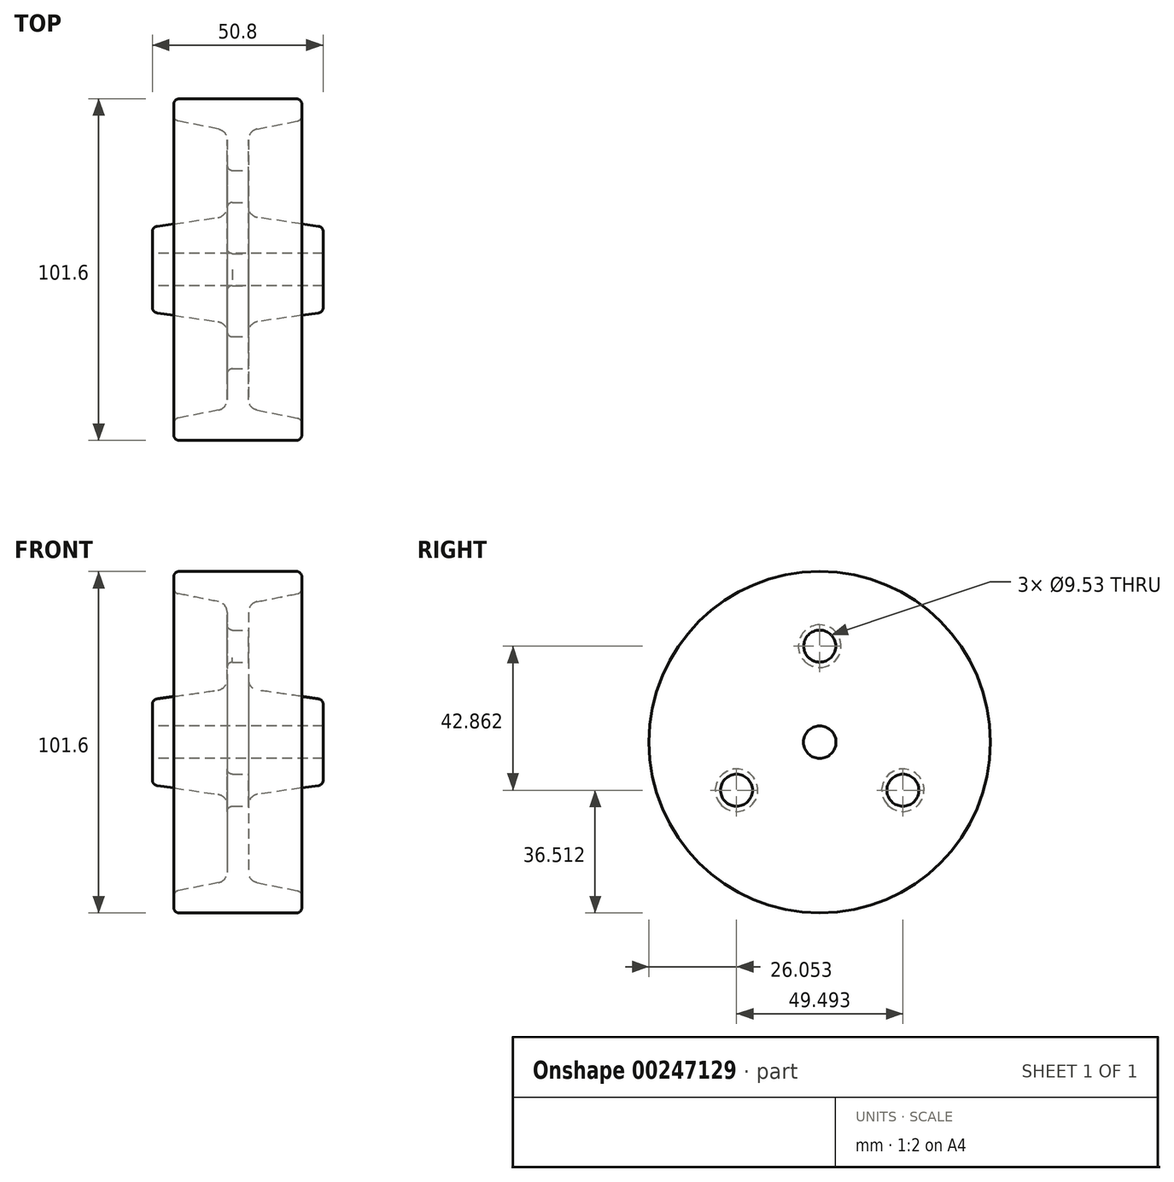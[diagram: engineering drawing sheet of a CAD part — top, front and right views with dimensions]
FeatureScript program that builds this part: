
annotation { "Feature Type Name" : "Feature", "Feature Type Description" : "" }
export const myFeature = defineFeature(function(context is Context, id is Id, definition is map)
    precondition{}
    {
        {
            var Q0;
            Q0=qCreatedBy(makeId("Front.planeOp"),FACE);
            var sketch = newSketch(context, id + "F0", { "sketchPlane" : qUnion([Q0])});
            skLineSegment(sketch, "E0", {"start": v(-25.03, 50.8) * mm, "end": v(9.9, 50.8) * mm});
            skLineSegment(sketch, "E1", {"start": v(-32.97, 4.83) * mm, "end": v(17.83, 4.83) * mm});
            skPoint(sketch, "E2", {"position": v(-7.57, 50.8) * mm});
            skPoint(sketch, "E3", {"position": v(-7.57, 4.83) * mm});
            skLineSegment(sketch, "E4", {"start": v(-32.97, 4.83) * mm, "end": v(-32.97, 11.32) * mm});
            skLineSegment(sketch, "E5", {"start": v(-26.62, 49.21) * mm, "end": v(-26.62, 45.75) * mm});
            skLineSegment(sketch, "E6", {"start": v(-7.57, 4.83) * mm, "end": v(-10.75, 4.83) * mm});
            skLineSegment(sketch, "E7", {"start": v(-7.57, 4.83) * mm, "end": v(-4.4, 4.83) * mm});
            skLineSegment(sketch, "E8", {"start": v(-31.6, 12.9) * mm, "end": v(-13.47, 15.49) * mm});
            skLineSegment(sketch, "E9", {"start": v(17.83, 4.83) * mm, "end": v(17.83, 11.32) * mm});
            skLineSegment(sketch, "E10", {"start": v(-1.67, 15.49) * mm, "end": v(16.47, 12.9) * mm});
            skLineSegment(sketch, "E11", {"start": v(-7.57, 50.8) * mm, "end": v(-10.75, 50.8) * mm});
            skLineSegment(sketch, "E12", {"start": v(-7.57, 50.8) * mm, "end": v(-4.4, 50.8) * mm});
            skLineSegment(sketch, "E13", {"start": v(-13.3, 41.79) * mm, "end": v(-25.35, 44.2) * mm});
            skLineSegment(sketch, "E14", {"start": v(11.48, 49.21) * mm, "end": v(11.48, 45.75) * mm});
            skLineSegment(sketch, "E15", {"start": v(-1.84, 41.79) * mm, "end": v(10.2, 44.2) * mm});
            skLineSegment(sketch, "E16", {"start": v(-10.75, 38.67) * mm, "end": v(-10.75, 34.92) * mm});
            skPoint(sketch, "E17.startSnap0", {"position": v(-10.75, 28.58) * mm});
            skLineSegment(sketch, "E18", {"start": v(-32.97, 4.83) * mm, "end": v(-32.97, 0) * mm});
            skLineSegment(sketch, "E19", {"start": v(-4.4, 18.63) * mm, "end": v(-4.4, 22.23) * mm});
            skLineSegment(sketch, "E20", {"start": v(-4.4, 38.67) * mm, "end": v(-4.4, 34.92) * mm});
            skLineSegment(sketch, "E21", {"start": v(-5.98, 33.34) * mm, "end": v(-9.16, 33.34) * mm});
            skLineSegment(sketch, "E22", {"start": v(-5.98, 23.81) * mm, "end": v(-9.16, 23.81) * mm});
            skLineSegment(sketch, "E23.trimOffspring", {"start": v(-10.75, 22.22) * mm, "end": v(-10.75, 18.63) * mm});
            skLineSegment(sketch, "E24", {"start": v(17.83, 4.83) * mm, "end": v(17.83, 0) * mm});
            skPoint(sketch, "E25.visualSharp", {"position": v(-10.75, 41.28) * mm});
            skArc(sketch, "E25.filletArc", {"start": v(-10.75, 38.67) * mm, "mid": v(-11.47, 40.69) * mm, "end": v(-13.3, 41.79) * mm});
            skPoint(sketch, "E26.visualSharp", {"position": v(-4.4, 41.28) * mm});
            skArc(sketch, "E26.filletArc", {"start": v(-1.84, 41.79) * mm, "mid": v(-3.68, 40.69) * mm, "end": v(-4.4, 38.67) * mm});
            skPoint(sketch, "E27.visualSharp", {"position": v(-4.4, 15.88) * mm});
            skArc(sketch, "E27.filletArc", {"start": v(-4.4, 18.63) * mm, "mid": v(-3.62, 16.55) * mm, "end": v(-1.67, 15.49) * mm});
            skPoint(sketch, "E28.visualSharp", {"position": v(-10.75, 15.88) * mm});
            skArc(sketch, "E28.filletArc", {"start": v(-13.47, 15.49) * mm, "mid": v(-11.52, 16.55) * mm, "end": v(-10.75, 18.63) * mm});
            skLineSegment(sketch, "E29", {"start": v(-32.97, 0) * mm, "end": v(-24.37, 0) * mm});
            skPoint(sketch, "E30.visualSharp", {"position": v(-26.62, 50.8) * mm});
            skArc(sketch, "E30.filletArc", {"start": v(-25.03, 50.8) * mm, "mid": v(-26.16, 50.34) * mm, "end": v(-26.62, 49.21) * mm});
            skPoint(sketch, "E31.visualSharp", {"position": v(-26.62, 44.45) * mm});
            skArc(sketch, "E31.filletArc", {"start": v(-26.62, 45.75) * mm, "mid": v(-26.26, 44.74) * mm, "end": v(-25.35, 44.2) * mm});
            skPoint(sketch, "E32.visualSharp", {"position": v(11.48, 50.8) * mm});
            skArc(sketch, "E32.filletArc", {"start": v(11.48, 49.21) * mm, "mid": v(11.01, 50.34) * mm, "end": v(9.9, 50.8) * mm});
            skPoint(sketch, "E33.visualSharp", {"position": v(11.48, 44.45) * mm});
            skArc(sketch, "E33.filletArc", {"start": v(10.2, 44.2) * mm, "mid": v(11.12, 44.74) * mm, "end": v(11.48, 45.75) * mm});
            skPoint(sketch, "E34.visualSharp", {"position": v(-10.75, 33.34) * mm});
            skArc(sketch, "E34.filletArc", {"start": v(-10.75, 34.92) * mm, "mid": v(-10.28, 33.8) * mm, "end": v(-9.16, 33.34) * mm});
            skPoint(sketch, "E35.visualSharp", {"position": v(-4.4, 33.34) * mm});
            skArc(sketch, "E35.filletArc", {"start": v(-5.98, 33.34) * mm, "mid": v(-4.86, 33.8) * mm, "end": v(-4.4, 34.92) * mm});
            skPoint(sketch, "E36.visualSharp", {"position": v(-10.75, 23.81) * mm});
            skArc(sketch, "E36.filletArc", {"start": v(-9.16, 23.81) * mm, "mid": v(-10.28, 23.35) * mm, "end": v(-10.75, 22.22) * mm});
            skPoint(sketch, "E37.visualSharp", {"position": v(-4.4, 23.81) * mm});
            skArc(sketch, "E37.filletArc", {"start": v(-4.4, 22.23) * mm, "mid": v(-4.86, 23.35) * mm, "end": v(-5.98, 23.81) * mm});
            skPoint(sketch, "E38.visualSharp", {"position": v(-32.97, 12.7) * mm});
            skArc(sketch, "E38.filletArc", {"start": v(-31.6, 12.9) * mm, "mid": v(-32.58, 12.36) * mm, "end": v(-32.97, 11.32) * mm});
            skPoint(sketch, "E39.visualSharp", {"position": v(17.83, 12.7) * mm});
            skArc(sketch, "E39.filletArc", {"start": v(17.83, 11.32) * mm, "mid": v(17.44, 12.36) * mm, "end": v(16.47, 12.9) * mm});
            skLineSegment(sketch, "E40", {"start": v(-10.75, 34.92) * mm, "end": v(-10.75, 22.22) * mm});
            skLineSegment(sketch, "E41", {"start": v(-4.4, 34.92) * mm, "end": v(-4.4, 22.23) * mm});
            skSolve(sketch);
        }
        {
            var Q0;
            Q0 = qSketchRegion(id + "F0", true);
            var Q1;
            Q1=sQuery(id+"F0.wireOp",EDGE,"E29");
            revolve(context, id + "F1", {"entities" : qUnion([Q0]), "axis" : qUnion([Q1]), "revolveType" : RevolveType.FULL});
        }
        {
            var Q0;
            Q0=makeQuery(id+"F1.opRevolve","SWEPT_FACE",FACE,{"disambiguationData":[OSD([sQuery(id+"F0.wireOp",EDGE,"E19"),sQuery(id+"F0.wireOp",EDGE,"E20"),sQuery(id+"F0.wireOp",EDGE,"E41")])]});
            var sketch = newSketch(context, id + "F2", { "sketchPlane" : qUnion([Q0])});
            skArc(sketch, "E42", {"start": v(-4.75, 28.18) * mm, "mid": v(-24.75, 14.29) * mm, "end": v(-26.78, -9.98) * mm});
            skCircle(sketch, "E43", {"center": v(0, 28.58) * mm, "radius": 4.76 * mm});
            skCircle(sketch, "E44.1.0", {"center": v(-24.75, -14.29) * mm, "radius": 4.76 * mm});
            skCircle(sketch, "E44.2.0", {"center": v(24.75, -14.29) * mm, "radius": 4.76 * mm});
            skArc(sketch, "E45.trimOffspring", {"start": v(-22.03, -18.2) * mm, "mid": v(0, -28.58) * mm, "end": v(22.03, -18.2) * mm});
            skArc(sketch, "E46.trimOffspring", {"start": v(26.78, -9.98) * mm, "mid": v(24.75, 14.29) * mm, "end": v(4.75, 28.18) * mm});
            skSolve(sketch);
        }
        {
            var Q0;
            {var subQ0=sQuery(id+"F2.wireOp",EDGE,"E43");var subQ1=makeQuery(id+"F2.imprint","INTERSECT",VERTEX,{"derivedFrom":[sQuery(id+"F2.wireOp",EDGE,"E42"),subQ0]});Q0=makeQuery(id+"F2.imprint","IMPRINT",FACE,{"disambiguationData":[TD([[makeQuery(id+"F2.imprint","IMPRINT",EDGE,{"disambiguationData":[TD([[subQ1,-1.0]])],"derivedFrom":subQ0}),1.0]])]});}
            var Q1;
            {var subQ0=sQuery(id+"F2.wireOp",EDGE,"E44.2.0");var subQ1=makeQuery(id+"F2.imprint","INTERSECT",VERTEX,{"derivedFrom":[subQ0,sQuery(id+"F2.wireOp",EDGE,"E45.trimOffspring")]});Q1=makeQuery(id+"F2.imprint","IMPRINT",FACE,{"disambiguationData":[TD([[makeQuery(id+"F2.imprint","IMPRINT",EDGE,{"disambiguationData":[TD([[subQ1,1.0]])],"derivedFrom":subQ0}),1.0]])]});}
            var Q2;
            {var subQ0=sQuery(id+"F2.wireOp",EDGE,"E44.1.0");var subQ1=makeQuery(id+"F2.imprint","INTERSECT",VERTEX,{"derivedFrom":[sQuery(id+"F2.wireOp",EDGE,"E42"),subQ0]});Q2=makeQuery(id+"F2.imprint","IMPRINT",FACE,{"disambiguationData":[TD([[makeQuery(id+"F2.imprint","IMPRINT",EDGE,{"disambiguationData":[TD([[subQ1,1.0]])],"derivedFrom":subQ0}),1.0]])]});}
            extrude(context, id + "F3", {"entities" : qUnion([Q0, Q1, Q2]), "operationType" : NewBodyOperationType.REMOVE, "oppositeDirection" : true, "depth" : 25.4 * mm});
        }
        {
            var Q0;
            Q0=makeQuery(id+"F3.boolean.opBoolean","INTERSECT",EDGE,{"derivedFrom":[makeQuery(id+"F1.opRevolve","SWEPT_FACE",FACE,{"disambiguationData":[OSD([sQuery(id+"F0.wireOp",EDGE,"E16"),sQuery(id+"F0.wireOp",EDGE,"E23.trimOffspring"),sQuery(id+"F0.wireOp",EDGE,"E40")])]}),makeQuery(id+"F3.opExtrude","SWEPT_FACE",FACE,{"disambiguationData":[OSD([sQuery(id+"F2.wireOp",EDGE,"E44.2.0")])]})]});
            var Q1;
            Q1=makeQuery(id+"F3.boolean.opBoolean","INTERSECT",EDGE,{"derivedFrom":[makeQuery(id+"F1.opRevolve","SWEPT_FACE",FACE,{"disambiguationData":[OSD([sQuery(id+"F0.wireOp",EDGE,"E16"),sQuery(id+"F0.wireOp",EDGE,"E23.trimOffspring"),sQuery(id+"F0.wireOp",EDGE,"E40")])]}),makeQuery(id+"F3.opExtrude","SWEPT_FACE",FACE,{"disambiguationData":[OSD([sQuery(id+"F2.wireOp",EDGE,"E43")])]})]});
            var Q2;
            Q2=makeQuery(id+"F3.boolean.opBoolean","INTERSECT",EDGE,{"derivedFrom":[makeQuery(id+"F1.opRevolve","SWEPT_FACE",FACE,{"disambiguationData":[OSD([sQuery(id+"F0.wireOp",EDGE,"E16"),sQuery(id+"F0.wireOp",EDGE,"E23.trimOffspring"),sQuery(id+"F0.wireOp",EDGE,"E40")])]}),makeQuery(id+"F3.opExtrude","SWEPT_FACE",FACE,{"disambiguationData":[OSD([sQuery(id+"F2.wireOp",EDGE,"E44.1.0")])]})]});
            var Q3;
            Q3=makeQuery(id+"F3.boolean.opBoolean","COPY",EDGE,{"derivedFrom":makeQuery(id+"F3.opExtrude","CAP_EDGE",EDGE,{"disambiguationData":[OSD([sQuery(id+"F2.wireOp",EDGE,"E44.1.0")])],"isStart":true})});
            var Q4;
            Q4=makeQuery(id+"F3.boolean.opBoolean","COPY",EDGE,{"derivedFrom":makeQuery(id+"F3.opExtrude","CAP_EDGE",EDGE,{"disambiguationData":[OSD([sQuery(id+"F2.wireOp",EDGE,"E43")])],"isStart":true})});
            var Q5;
            Q5=makeQuery(id+"F3.boolean.opBoolean","COPY",EDGE,{"derivedFrom":makeQuery(id+"F3.opExtrude","CAP_EDGE",EDGE,{"disambiguationData":[OSD([sQuery(id+"F2.wireOp",EDGE,"E44.2.0")])],"isStart":true})});
            fillet(context, id + "F4", {"entities" : qUnion([Q0, Q1, Q2, Q3, Q4, Q5]), "radius" : 1.59 * mm, "tangentPropagation" : true, "allowEdgeOverflow" : false});
        }
    });
